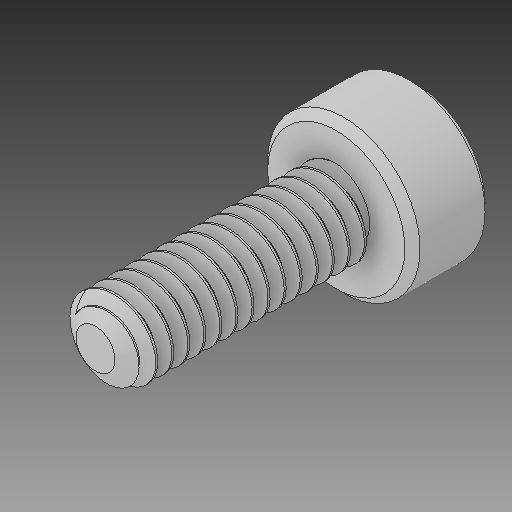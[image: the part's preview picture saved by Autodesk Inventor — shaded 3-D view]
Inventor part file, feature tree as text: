
AUTODESK INVENTOR PART (.ipt)
format: ipt  version: 2018 (Build 220112000, 112)  size: 645,120 bytes
history: native  units: in
note: dims shown in document units (in); Inventor stores cm internally (conversion verified against a paired STEP export)
features: chamfer x1
ambient origin geometry x8: Origin, YZ Plane, XZ Plane, XY Plane, X Axis, Y Axis, Z Axis, Center Point
bodies: Solid1 (feature_tree)
feature tree (1):
  chamfer  "Chamfer1"  [1 undecoded]
note: 1 required parameter value undecoded (feature->parameter linkage not recoverable at this tier; creation-order binding heuristic only, values carry confidence <= 0.55)
